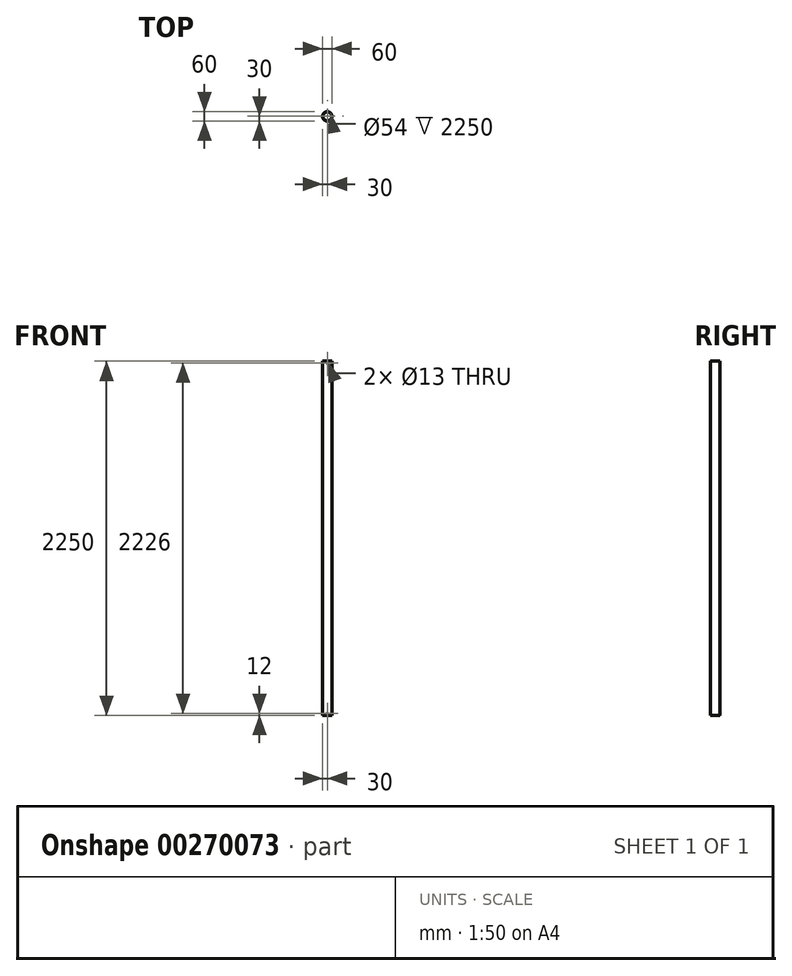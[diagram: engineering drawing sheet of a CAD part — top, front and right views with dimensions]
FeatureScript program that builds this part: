
annotation { "Feature Type Name" : "Feature", "Feature Type Description" : "" }
export const myFeature = defineFeature(function(context is Context, id is Id, definition is map)
    precondition{}
    {
        {
            var Q0;
            Q0=qCreatedBy(makeId("Top.planeOp"),FACE);
            var sketch = newSketch(context, id + "F0", { "sketchPlane" : qUnion([Q0])});
            skCircle(sketch, "E0", {"center": v(0, 0) * mm, "radius": 30 * mm});
            skCircle(sketch, "E1.0", {"center": v(0, 0) * mm, "radius": 27 * mm});
            skSolve(sketch);
        }
        {
            var Q0;
            Q0=makeQuery(id+"F0.imprint","IMPRINT",FACE,{"disambiguationData":[TD([[makeQuery(id+"F0.imprint","IMPRINT",EDGE,{"derivedFrom":sQuery(id+"F0.wireOp",EDGE,"E0")}),1.0]])]});
            extrude(context, id + "F1", {"entities" : qUnion([Q0]), "depth" : 2250 * mm});
        }
        {
            var Q0;
            Q0=qCreatedBy(makeId("Front.planeOp"),FACE);
            var sketch = newSketch(context, id + "F2", { "sketchPlane" : qUnion([Q0])});
            skCircle(sketch, "E2", {"center": v(0, 12) * mm, "radius": 6.5 * mm});
            skCircle(sketch, "E3", {"center": v(0, 2238) * mm, "radius": 6.5 * mm});
            skSolve(sketch);
        }
        {
            var Q0;
            Q0 = qSketchRegion(id + "F2", true);
            var Q1;
            Q1=sQuery(id+"F2.wireOp",EDGE,"E2");
            extrude(context, id + "F3", {"entities" : qUnion([Q0]), "operationType" : NewBodyOperationType.REMOVE, "surfaceEntities" : qUnion([Q1]), "oppositeDirection" : true, "depth" : 60 * mm});
        }
    });
